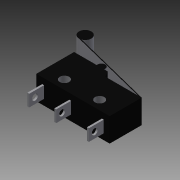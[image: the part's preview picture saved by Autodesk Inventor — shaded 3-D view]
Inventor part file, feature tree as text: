
AUTODESK INVENTOR PART (.ipt)
format: ipt  version: 2013 (Build 170138000, 138)  size: 162,304 bytes
history: native  units: mm
features: extrude x5, sketch x5
ambient origin geometry x8: Origin, YZ Plane, XZ Plane, XY Plane, X Axis, Y Axis, Z Axis, Center Point
bodies: Solid1 (feature_tree)
feature tree (10):
  extrude  "Extrusion1"  Depth=6.4mm TaperAngle=0.0deg
  extrude  "Extrusion3"  Depth=6.4mm TaperAngle=0.0deg
  extrude  "Extrusion4"  Depth=1.6mm
  extrude  "Extrusion5"  Depth=6.4mm TaperAngle=0.0deg
  extrude  "Extrusion2"  [1 undecoded]
  sketch  "Sketch1"  dims[d0=9.1mm d1=10.2mm d2=19.8mm d3=2.5mm d4=5.1mm d5=2.5mm d6=9.5mm d7=2.5mm d8=2.5mm d9=2.0mm d10=7.5mm d11=10.5mm d12=6.4mm d13=0.0mm]
  sketch  "Sketch2"  dims[d14=0.5mm d15=4.0mm d16=0.5mm d17=0.5mm d18=8.3mm d19=6.8mm d20=6.4mm d21=0.0mm]
  sketch  "Sketch3"  dims[d22=4.0mm d23=0.0mm d24=1.6mm]
  sketch  "Sketch4"  dims[d26=22.0mm d27=0.0mm d28=6.4mm d29=0.0mm]
  sketch  "Sketch5"
note: 1 required parameter value undecoded (feature->parameter linkage not recoverable at this tier; creation-order binding heuristic only, values carry confidence <= 0.55)
